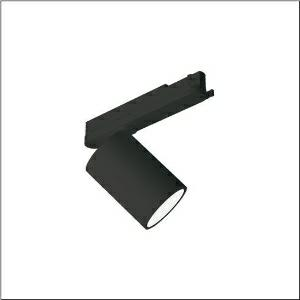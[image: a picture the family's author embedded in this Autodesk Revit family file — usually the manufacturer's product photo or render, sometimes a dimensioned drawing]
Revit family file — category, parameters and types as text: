
# Revit family: spot_31_51sf32mab4b
name_source: partatom
category: Lighting Fixtures
units: mm (PartAtom-declared; Revit-internal decimal feet)

## family parameters
Cut with Voids When Loaded = No
Host = Face
Light Source = No
Part Type = Normal
Room Calculation Point = No
Round Connector Dimension = Use Diameter
Shared = No

## types (1)
- --- (1 x LED, 4980 lm, 41.8 W, 3000K)
    Apparent Load = 42 VA
    CIE Flux Codes = 93 97 99 100 100
    Color Rendering = 90
    Color Temperature = 3000K
    Default Elevation = 1800 mm
    Description = Spot 31, directional spotlight, light control with lens, of PMMA, LED rated luminous flux: 4.790lm, light colour: 930, control gear: ECG Multilumen, with 3-phase adapter, mains connection: 220..240V, AC, 50/60Hz, of aluminium, jet black (RAL 9005), length: 213mm, diameter: 90mm, protection rating (complete): IP20, insulation class (complete): insulation class I (protective earthing), certification: CE, impact resistance: IK02, permissible ambient temperature for indoor applications: -20..+40°C, packaging unit: 1 piece
    Height = 175 mm
    Lamp = 1 x LED
    Lamp Light Flux = 4980 lm
    Lamp Power = 41.8 W
    Lamp count = 1
    Length = 90 mm
    Luminous efficacy = 119 lm/W
    Manufacturer = Siteco
    ModVariant = No
    Model = 51SF32MAB4B
    Mounting Place = Ceiling
    Mounting Type = Pendant
    Number of Poles = 1
    OnlyDefault = Yes
    Power Factor = 1
    Product Name = Spot 31
    Product group = directional spotlight
    ProductGroupID = 906
    Protection Class = Protection class I
    Protection Degree = IP 20
    RLX_Detail_Level = 1
    RLX_Emergency_Light_Flux = 0 lm
    RLX_Emergency_Type = 0
    RLX_Emergency_Type_DB = No
    RlxData = <blob elided: 20913 chars, md5=182b74d2>
    Socket = socket
    Standby Power = 0 W
    System Light Flux = 4980 lm
    System Power = 42 W
    Type Comments = factory setting: luminous flux: 100 % | (ON | ON | ON | ON) | 1050 mA
    Type Image = l_1273723.jpg
    URL = http://relux.com
    VarID = @adj_146634
    Voltage = 0 V
    Weight = 0.00 kg
    Width = 0 mm  [stored 0 ft]

note: [stored X ft] marks values corroborated as IEEE doubles in the binary element streams (Revit-internal decimal feet)

## geometry (parser evidence)
native form markers: Blend x4, Sweep x9
no freeform markers — native parametric forms only
